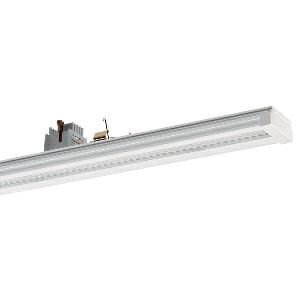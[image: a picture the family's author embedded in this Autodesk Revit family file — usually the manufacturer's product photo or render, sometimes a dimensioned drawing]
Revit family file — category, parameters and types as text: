
# Revit family: conveo_-_cvg_8000_840_xn-l_ea_5_226848459-00804984_df4d
name_source: partatom
category: Lighting Fixtures
units: mm (PartAtom-declared; Revit-internal decimal feet)

## family parameters
Cut with Voids When Loaded = No
Host = Face
Light Source = No
Part Type = Normal
Room Calculation Point = No
Round Connector Dimension = Use Diameter
Shared = No

## types (1)
- CONVEO - CVG 8000/840/xN-L/EA/5 (1 x LED, 8450 lm, 4000K)
    Apparent Load = 51 VA
    Approval mark = CE
    CIE Flux Codes = 84 95 99 100 100
    Color Rendering = 80-89
    Color Temperature = 4000K
    Control Gear = Electronic ballast
    Default Elevation = 1800 mm
    Description = CVG 8000/840/xN-L/EA/5|Continuous-row system|light source: LED|work equipment: Electronic ballast|connected load: 220-240 V, 50-60 Hz|Power consumption: approx. 51 W|luminous flux: 8450 lm|luminous efficacy: 165 lm/W|colour temperature: Cold white, ca. 4000 K|color rendering index (CRI): >= 80|chromaticity tolerance:  3 SDCM|System of protection: IP 54|class of protection: I|technology: Switchable|luminaire body|material: Aluminium|surface: Powder coatet|colour: White|lamp cover: Acrylic (PMMA), Satine|weight (net): approx. 1.9 kg|Fastening: Available separately|maximum ambient temperature: 46 ░C|glare control: Lens optics|Approval mark: VDE - ENEC|
    Frequency = 50 Hz
    Height = 70 mm
    Lamp = 1 x LED
    Lamp Light Flux = 8450 lm
    Lamp count = 1
    Length = 1500 mm
    Luminous efficacy = 166 lm/W
    Manufacturer = Waldmann
    ModVariant = No
    Model = 226848459-00804984
    Mounting Place = Ceiling
    Mounting Type = Pendant
    Number of Poles = 1
    OnlyDefault = Yes
    Power Factor = 1
    Product Name = CONVEO - CVG 8000/840/xN-L/EA/5
    Product group = Continuous-row system (industry)
    ProductGroupID = 301
    Protection Class = Protection class I
    Protection Degree = IP 54
    RLX_Detail_Level = 1
    RlxData = <blob elided: 100469 chars, md5=effaeabd>
    Socket = socket
    Standby Power = 0 W
    System Light Flux = 8450 lm
    System Power = 51 W
    Type Comments = Product without accessories
    Type Image = 226848319-00804970_1l5.jpg
    URL = http://relux.com
    VarID = ---
    Voltage = 230 V
    Voltage Range = 220-240 V
    Weight = 0.00 kg
    Width = 64 mm

## geometry (parser evidence)
native form markers: Blend x4, Sweep x11
no freeform markers — native parametric forms only
